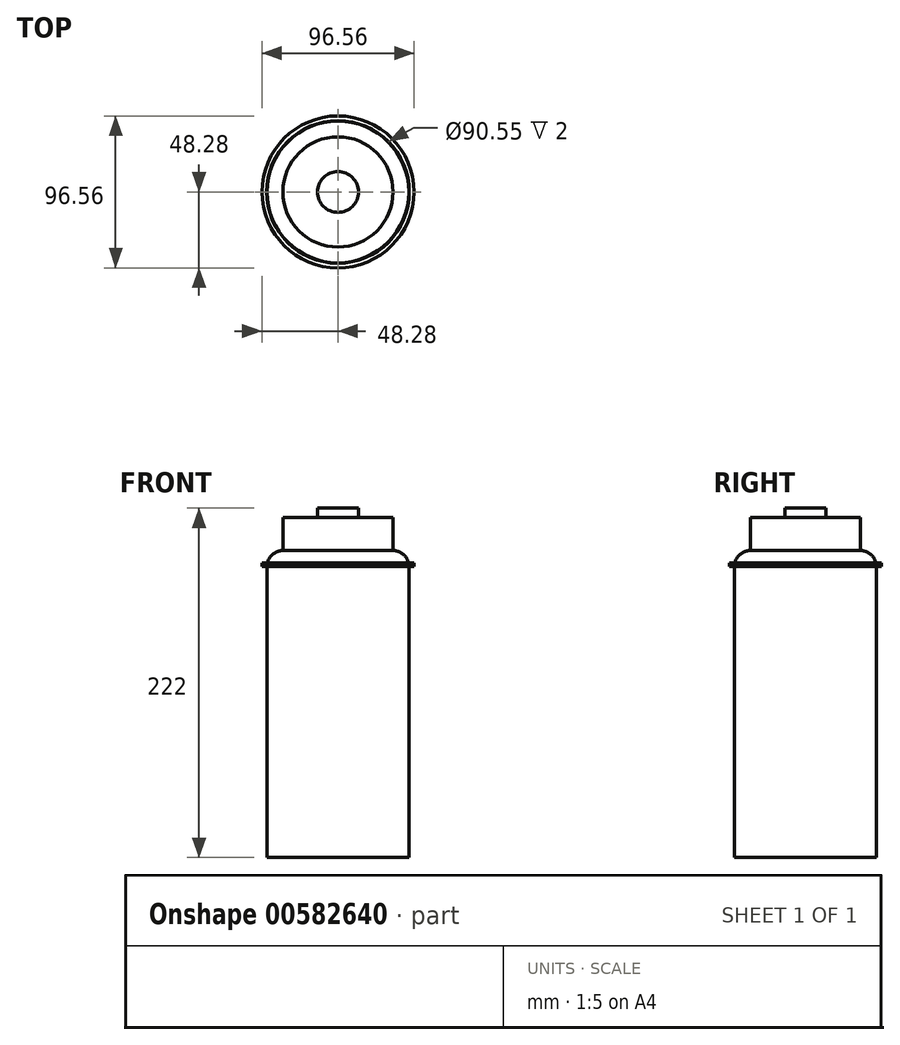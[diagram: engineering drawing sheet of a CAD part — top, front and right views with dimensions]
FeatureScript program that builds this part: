
annotation { "Feature Type Name" : "Feature", "Feature Type Description" : "" }
export const myFeature = defineFeature(function(context is Context, id is Id, definition is map)
    precondition{}
    {
        {
            var Q0;
            Q0=qCreatedBy(makeId("Top.planeOp"),FACE);
            var sketch = newSketch(context, id + "F0", { "sketchPlane" : qUnion([Q0])});
            skCircle(sketch, "E0", {"center": v(0, 0) * mm, "radius": 45 * mm});
            skSolve(sketch);
        }
        {
            var Q0;
            Q0=makeQuery(id+"F0.imprint","IMPRINT",FACE,{"disambiguationData":[TD([[makeQuery(id+"F0.imprint","IMPRINT",EDGE,{"derivedFrom":sQuery(id+"F0.wireOp",EDGE,"E0")}),1.0]])]});
            extrude(context, id + "F1", {"entities" : qUnion([Q0]), "depth" : 195 * mm, "offsetDistance" : 25.4 * mm});
        }
        {
            var Q0;
            Q0=makeQuery(id+"F1.opExtrude","CAP_FACE",FACE,{"disambiguationData":[OSD([sQuery(id+"F0.wireOp",EDGE,"E0")])],"isStart":false});
            fillet(context, id + "F2", {"entities" : qUnion([Q0]), "radius" : 10 * mm, "tangentPropagation" : true, "allowEdgeOverflow" : false});
        }
        {
            var Q0;
            Q0=makeQuery(id+"F1.opExtrude","CAP_FACE",FACE,{"disambiguationData":[OSD([sQuery(id+"F0.wireOp",EDGE,"E0")])],"isStart":false});
            var sketch = newSketch(context, id + "F3", { "sketchPlane" : qUnion([Q0])});
            skCircle(sketch, "E1", {"center": v(0, 0) * mm, "radius": 35 * mm});
            skSolve(sketch);
        }
        {
            var Q0;
            Q0=makeQuery(id+"F3.imprint","IMPRINT",FACE,{"disambiguationData":[TD([[makeQuery(id+"F3.imprint","IMPRINT",EDGE,{"derivedFrom":sQuery(id+"F3.wireOp",EDGE,"E1")}),1.0]])]});
            extrude(context, id + "F4", {"entities" : qUnion([Q0]), "operationType" : NewBodyOperationType.ADD, "depth" : 21 * mm, "offsetDistance" : 25 * mm});
        }
        {
            var Q0;
            Q0=qCreatedBy(makeId("Front.planeOp"),FACE);
            var sketch = newSketch(context, id + "F5", { "sketchPlane" : qUnion([Q0])});
            skLineSegment(sketch, "E2.bottom", {"start": v(-45.28, 185) * mm, "end": v(-48.28, 185) * mm});
            skLineSegment(sketch, "E2.top", {"start": v(-45.28, 187) * mm, "end": v(-48.28, 187) * mm});
            skLineSegment(sketch, "E2.left", {"start": v(-45.28, 185) * mm, "end": v(-45.28, 187) * mm});
            skLineSegment(sketch, "E2.right", {"start": v(-48.28, 185) * mm, "end": v(-48.28, 187) * mm});
            skSolve(sketch);
        }
        {
            var Q0;
            Q0=makeQuery(id+"F5.imprint","IMPRINT",FACE,{"disambiguationData":[TD([[makeQuery(id+"F5.imprint","IMPRINT",EDGE,{"derivedFrom":sQuery(id+"F5.wireOp",EDGE,"E2.bottom")}),-1.0]])]});
            var Q1;
            Q1=makeQuery(id+"F2.opFillet","BLEND_FACE",FACE,{"disambiguationData":[OSD([sQuery(id+"F0.wireOp",EDGE,"E0")])]});
            revolve(context, id + "F6", {"entities" : qUnion([Q0]), "axis" : qUnion([Q1]), "revolveType" : RevolveType.FULL});
        }
        {
            var Q0;
            Q0=makeQuery(id+"F4.opExtrude","CAP_FACE",FACE,{"disambiguationData":[OSD([sQuery(id+"F3.wireOp",EDGE,"E1")])],"isStart":false});
            var sketch = newSketch(context, id + "F7", { "sketchPlane" : qUnion([Q0])});
            skCircle(sketch, "E3", {"center": v(0, 0) * mm, "radius": 13 * mm});
            skSolve(sketch);
        }
        {
            var Q0;
            Q0=makeQuery(id+"F7.imprint","IMPRINT",FACE,{"disambiguationData":[TD([[makeQuery(id+"F7.imprint","IMPRINT",EDGE,{"derivedFrom":sQuery(id+"F7.wireOp",EDGE,"E3")}),1.0]])]});
            extrude(context, id + "F8", {"entities" : qUnion([Q0]), "operationType" : NewBodyOperationType.ADD, "depth" : 3 * mm, "offsetDistance" : 25 * mm});
        }
        {
            var Q0;
            Q0=makeQuery(id+"F8.opExtrude","CAP_FACE",FACE,{"disambiguationData":[OSD([sQuery(id+"F7.wireOp",EDGE,"E3")])],"isStart":false});
            var sketch = newSketch(context, id + "F9", { "sketchPlane" : qUnion([Q0])});
            skCircle(sketch, "E4", {"center": v(0, 0) * mm, "radius": 13 * mm});
            skSolve(sketch);
        }
        {
            var Q0;
            Q0=makeQuery(id+"F9.imprint","IMPRINT",FACE,{"disambiguationData":[TD([[makeQuery(id+"F9.imprint","IMPRINT",EDGE,{"derivedFrom":sQuery(id+"F9.wireOp",EDGE,"E4")}),1.0]])]});
            extrude(context, id + "F10", {"entities" : qUnion([Q0]), "operationType" : NewBodyOperationType.ADD, "depth" : 3 * mm, "offsetDistance" : 25 * mm});
        }
    });
